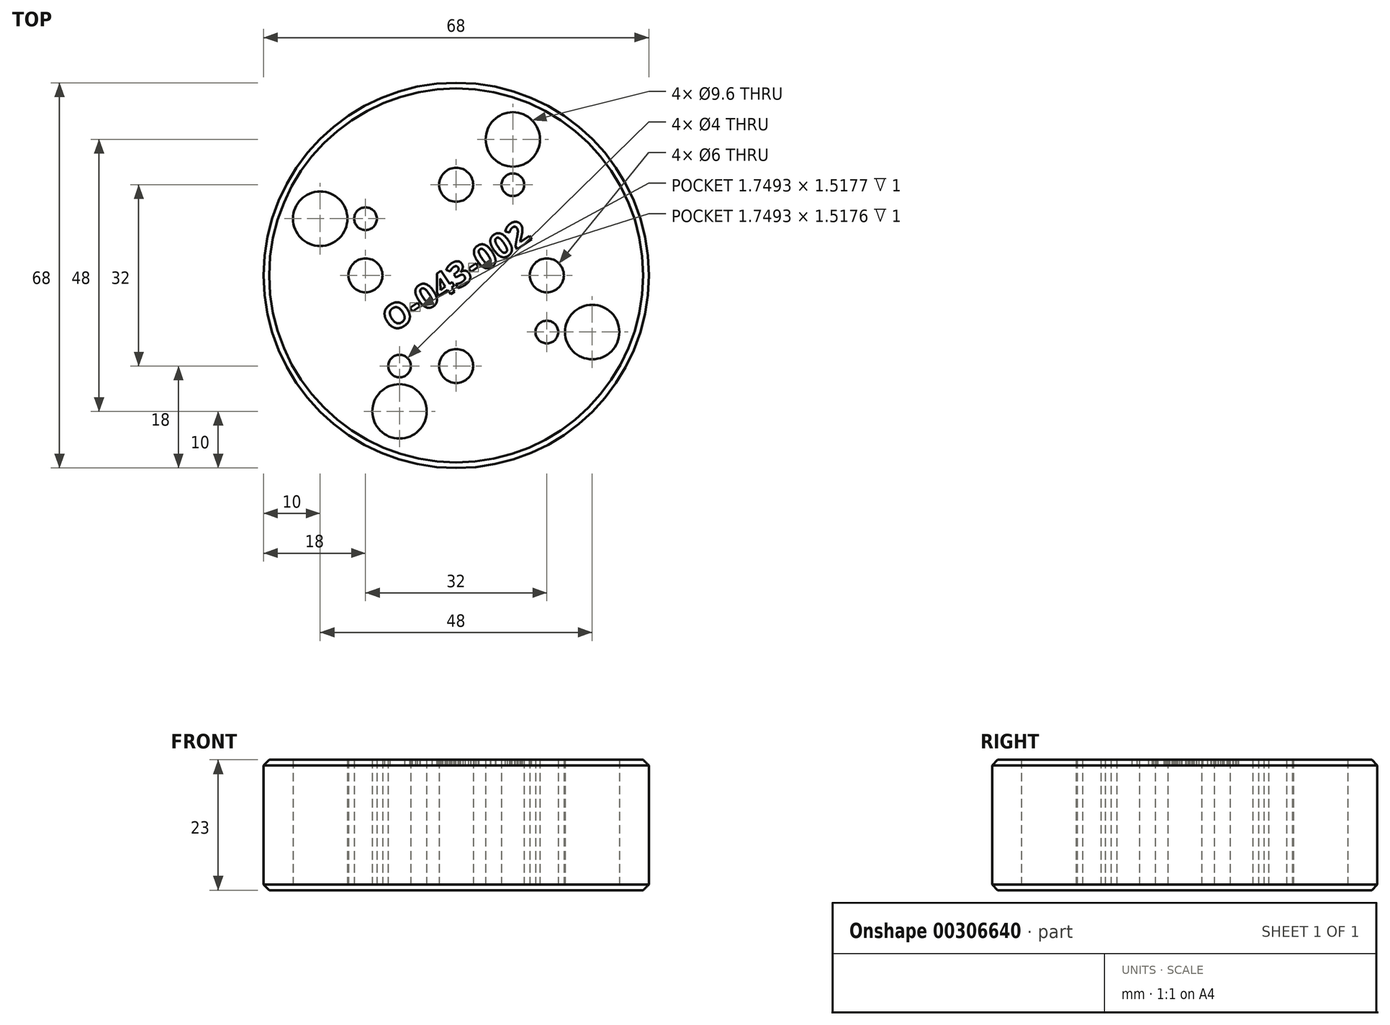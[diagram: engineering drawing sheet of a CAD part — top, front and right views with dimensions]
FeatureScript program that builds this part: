
annotation { "Feature Type Name" : "Feature", "Feature Type Description" : "" }
export const myFeature = defineFeature(function(context is Context, id is Id, definition is map)
    precondition{}
    {
        {
            var Q0;
            Q0=qCreatedBy(makeId("Top.planeOp"),FACE);
            var sketch = newSketch(context, id + "F0", { "sketchPlane" : qUnion([Q0])});
            skCircle(sketch, "E0", {"center": v(0, 16) * mm, "radius": 3 * mm});
            skPoint(sketch, "E1.center", {"position": v(0, 0) * mm});
            skCircle(sketch, "E2", {"center": v(10, 16) * mm, "radius": 2 * mm});
            skCircle(sketch, "E3.1.0", {"center": v(-16, 0) * mm, "radius": 3 * mm});
            skCircle(sketch, "E3.1.1", {"center": v(-16, 10) * mm, "radius": 2 * mm});
            skCircle(sketch, "E3.2.0", {"center": v(0, -16) * mm, "radius": 3 * mm});
            skCircle(sketch, "E3.2.1", {"center": v(-10, -16) * mm, "radius": 2 * mm});
            skCircle(sketch, "E3.3.0", {"center": v(16, 0) * mm, "radius": 3 * mm});
            skCircle(sketch, "E3.3.1", {"center": v(16, -10) * mm, "radius": 2 * mm});
            skCircle(sketch, "E4", {"center": v(0, 0) * mm, "radius": 25 * mm});
            skCircle(sketch, "E5", {"center": v(-24, 10) * mm, "radius": 4 * mm, "construction": true});
            skArc(sketch, "E6", {"start": v(-24.45, 5.22) * mm, "mid": v(-19.57, 8.15) * mm, "end": v(-20.92, 13.68) * mm});
            skCircle(sketch, "E7", {"center": v(-16, 10) * mm, "radius": 4.5 * mm, "construction": true});
            skArc(sketch, "E8.1.0", {"start": v(-5.22, -24.45) * mm, "mid": v(-8.15, -19.57) * mm, "end": v(-13.68, -20.92) * mm});
            skArc(sketch, "E8.2.0", {"start": v(24.45, -5.22) * mm, "mid": v(19.57, -8.15) * mm, "end": v(20.92, -13.68) * mm});
            skArc(sketch, "E8.3.0", {"start": v(5.22, 24.45) * mm, "mid": v(8.15, 19.57) * mm, "end": v(13.68, 20.92) * mm});
            skCircle(sketch, "E9", {"center": v(0, 0) * mm, "radius": 34 * mm});
            skCircle(sketch, "E10", {"center": v(-24, 10) * mm, "radius": 4.8 * mm});
            skCircle(sketch, "E11", {"center": v(10, 24) * mm, "radius": 4.8 * mm});
            skCircle(sketch, "E12", {"center": v(24, -10) * mm, "radius": 4.8 * mm});
            skCircle(sketch, "E13", {"center": v(-10, -24) * mm, "radius": 4.8 * mm});
            skLineSegment(sketch, "E14", {"start": v(0, 0) * mm, "end": v(10, 16) * mm, "construction": true});
            skLineSegment(sketch, "E15", {"start": v(0, 0) * mm, "end": v(10, 24) * mm, "construction": true});
            skSolve(sketch);
        }
        {
            var Q0;
            Q0=makeQuery(id+"F0.imprint","IMPRINT",FACE,{"disambiguationData":[TD([[makeQuery(id+"F0.imprint","IMPRINT",EDGE,{"derivedFrom":sQuery(id+"F0.wireOp",EDGE,"E1.2.1")}),1.0]])]});
            var Q1;
            Q1=makeQuery(id+"F0.imprint","IMPRINT",FACE,{"disambiguationData":[TD([[makeQuery(id+"F0.imprint","IMPRINT",EDGE,{"derivedFrom":sQuery(id+"F0.wireOp",EDGE,"E1.3.1")}),1.0]])]});
            var Q2;
            Q2=makeQuery(id+"F0.imprint","IMPRINT",FACE,{"disambiguationData":[TD([[makeQuery(id+"F0.imprint","IMPRINT",EDGE,{"derivedFrom":sQuery(id+"F0.wireOp",EDGE,"E1.3.0")}),1.0]])]});
            var Q3;
            Q3=makeQuery(id+"F0.imprint","IMPRINT",FACE,{"disambiguationData":[TD([[makeQuery(id+"F0.imprint","IMPRINT",EDGE,{"derivedFrom":sQuery(id+"F0.wireOp",EDGE,"E1.2.0")}),1.0]])]});
            var Q4;
            Q4=makeQuery(id+"F0.imprint","IMPRINT",FACE,{"disambiguationData":[TD([[makeQuery(id+"F0.imprint","IMPRINT",EDGE,{"derivedFrom":sQuery(id+"F0.wireOp",EDGE,"5VkqoSrS-Cs9u-Mvgf-fKKW-AaG6FBBb1eUr")}),1.0]])]});
            var Q5;
            Q5=makeQuery(id+"F0.imprint","IMPRINT",FACE,{"disambiguationData":[TD([[makeQuery(id+"F0.imprint","IMPRINT",EDGE,{"derivedFrom":sQuery(id+"F0.wireOp",EDGE,"E1.1.0")}),1.0]])]});
            var Q6;
            Q6=makeQuery(id+"F0.imprint","IMPRINT",FACE,{"disambiguationData":[TD([[makeQuery(id+"F0.imprint","IMPRINT",EDGE,{"derivedFrom":sQuery(id+"F0.wireOp",EDGE,"E1.1.1")}),1.0]])]});
            var Q7;
            Q7=makeQuery(id+"F0.imprint","IMPRINT",FACE,{"disambiguationData":[TD([[makeQuery(id+"F0.imprint","IMPRINT",EDGE,{"derivedFrom":sQuery(id+"F0.wireOp",EDGE,"E0")}),-1.0]])]});
            var Q8;
            Q8=makeQuery(id+"F0.imprint","IMPRINT",FACE,{"disambiguationData":[TD([[makeQuery(id+"F0.imprint","IMPRINT",EDGE,{"derivedFrom":sQuery(id+"F0.wireOp",EDGE,"E9")}),1.0]])]});
            extrude(context, id + "F1", {"entities" : qUnion([Q0, Q1, Q2, Q3, Q4, Q5, Q6, Q7, Q8]), "depth" : 23 * mm});
        }
        {
            var Q0;
            Q0=makeQuery(id+"F1.opExtrude","CAP_FACE",FACE,{"disambiguationData":[OSD([sQuery(id+"F0.wireOp",EDGE,"E0"),sQuery(id+"F0.wireOp",EDGE,"E2"),sQuery(id+"F0.wireOp",EDGE,"E3.1.0"),sQuery(id+"F0.wireOp",EDGE,"E3.1.1"),sQuery(id+"F0.wireOp",EDGE,"E3.2.0"),sQuery(id+"F0.wireOp",EDGE,"E3.2.1"),sQuery(id+"F0.wireOp",EDGE,"E3.3.0"),sQuery(id+"F0.wireOp",EDGE,"E3.3.1"),sQuery(id+"F0.wireOp",EDGE,"E4")])],"isStart":false});
            var sketch = newSketch(context, id + "F2", { "sketchPlane" : qUnion([Q0])});
            skText(sketch, "E16", { "text": "O-043-002", "fontName": "OpenSans-Bold.ttf"});
            skPoint(sketch, "E17", {"position": v(0, 0) * mm});
            const initialGuessF2  = {"E16": [-0.0112, -0.01022, 0.82904, 0.5592, 0.00441]};
            skSetInitialGuess(sketch, initialGuessF2);
            skSolve(sketch);
        }
        {
            var Q0;
            Q0=qSketchRegion(id+"F2",true);
            extrude(context, id + "F3", {"entities" : qUnion([Q0]), "operationType" : NewBodyOperationType.REMOVE, "oppositeDirection" : true, "depth" : 1 * mm});
        }
        {
            var Q0;
            Q0=makeQuery(id+"F1.opExtrude","CAP_EDGE",EDGE,{"disambiguationData":[OSD([sQuery(id+"F0.wireOp",EDGE,"E9")])],"isStart":false});
            var Q1;
            Q1=makeQuery(id+"F1.opExtrude","CAP_EDGE",EDGE,{"disambiguationData":[OSD([sQuery(id+"F0.wireOp",EDGE,"E9")])],"isStart":true});
            chamfer(context, id + "F4", {"entities" : qUnion([Q0, Q1]), "width" : 1 * mm, "tangentPropagation" : true});
        }
    });
